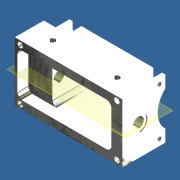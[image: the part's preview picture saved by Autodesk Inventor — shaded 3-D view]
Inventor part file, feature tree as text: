
AUTODESK INVENTOR PART (.ipt)
format: ipt  version: 2018 (Build 220112000, 112)  size: 304,128 bytes
history: native  units: mm
features: extrude x13, sketch x13, plane x1, mirror x1, fillet x1
ambient origin geometry x8: Origin, YZ Plane, XZ Plane, XY Plane, X Axis, Y Axis, Z Axis, Center Point
bodies: Solid1 (feature_tree)
feature tree (29):
  extrude  "Extrusion1"  Depth=100.0mm
  extrude  "Extrusion2"  Depth=5.0mm
  extrude  "Extrusion3"  Depth=5.0mm
  extrude  "Extrusion4"  Depth=2.5mm
  extrude  "Extrusion5"  Depth=40.0mm
  extrude  "Extrusion6"  Depth=7.5mm
  extrude  "Extrusion7"  Depth=10.0mm
  extrude  "Extrusion8"  Depth=10.0mm
  plane  "Work Plane1"
  mirror  "Mirror1"
  fillet  "Fillet1"  Radius=55.0mm
  extrude  "Extrusion9"  Depth=10.0mm
  extrude  "Extrusion10"  Depth=10.0mm
  extrude  "Extrusion11"  Depth=15.0mm
  extrude  "Extrusion12"  Depth=5.0mm
  extrude  "Extrusion13"  Depth=5.0mm
  sketch  "Sketch1"  dims[d0=55.0mm d1=100.0mm]
  sketch  "Sketch2"  dims[d2=40.0mm d3=0.0mm d4=5.0mm]
  sketch  "Sketch3"  dims[d5=5.0mm d6=3.75mm]
  sketch  "Sketch4"  dims[d7=18.0mm d8=0.0mm d9=2.5mm]
  sketch  "Sketch5"  dims[d10=87.5mm d11=40.0mm]
  sketch  "Sketch6"  dims[d12=55.0mm d13=7.5mm]
  sketch  "Sketch7"  dims[d14=10.0mm d15=0.0mm d16=65.0mm]
  sketch  "Sketch8"  dims[d17=10.0mm d18=0.0mm d19=27.5mm d20=55.0mm]
  sketch  "Sketch10"  dims[d21=10.0mm d22=16.0mm]
  sketch  "Sketch11"  dims[d23=10.0mm d24=0.0mm d25=15.0mm]
  sketch  "Sketch12"  dims[d26=1.0mm d27=0.0mm d28=15.0mm]
  sketch  "Sketch13"  dims[d29=1.0mm d30=0.0mm d31=5.0mm]
  sketch  "Sketch15"  dims[d32=20.0mm d33=15.0mm d34=5.0mm d35=20.0mm d36=15.0mm d37=15.0mm d38=0.0mm d39=5.0mm d40=8.0mm d41=7.0mm d43=8.0mm d44=7.0mm d45=7.0mm d46=8.0mm d47=0.0mm d48=82.0mm d49=4.0mm d50=5.5mm d51=5.5mm d52=13.0mm d53=0.0mm d54=3.0mm d55=13.0mm d56=0.0mm d57=13.0mm d58=0.0mm d59=27.5mm d60=15.0mm d61=44.0mm d62=13.0mm d63=0.0mm]
